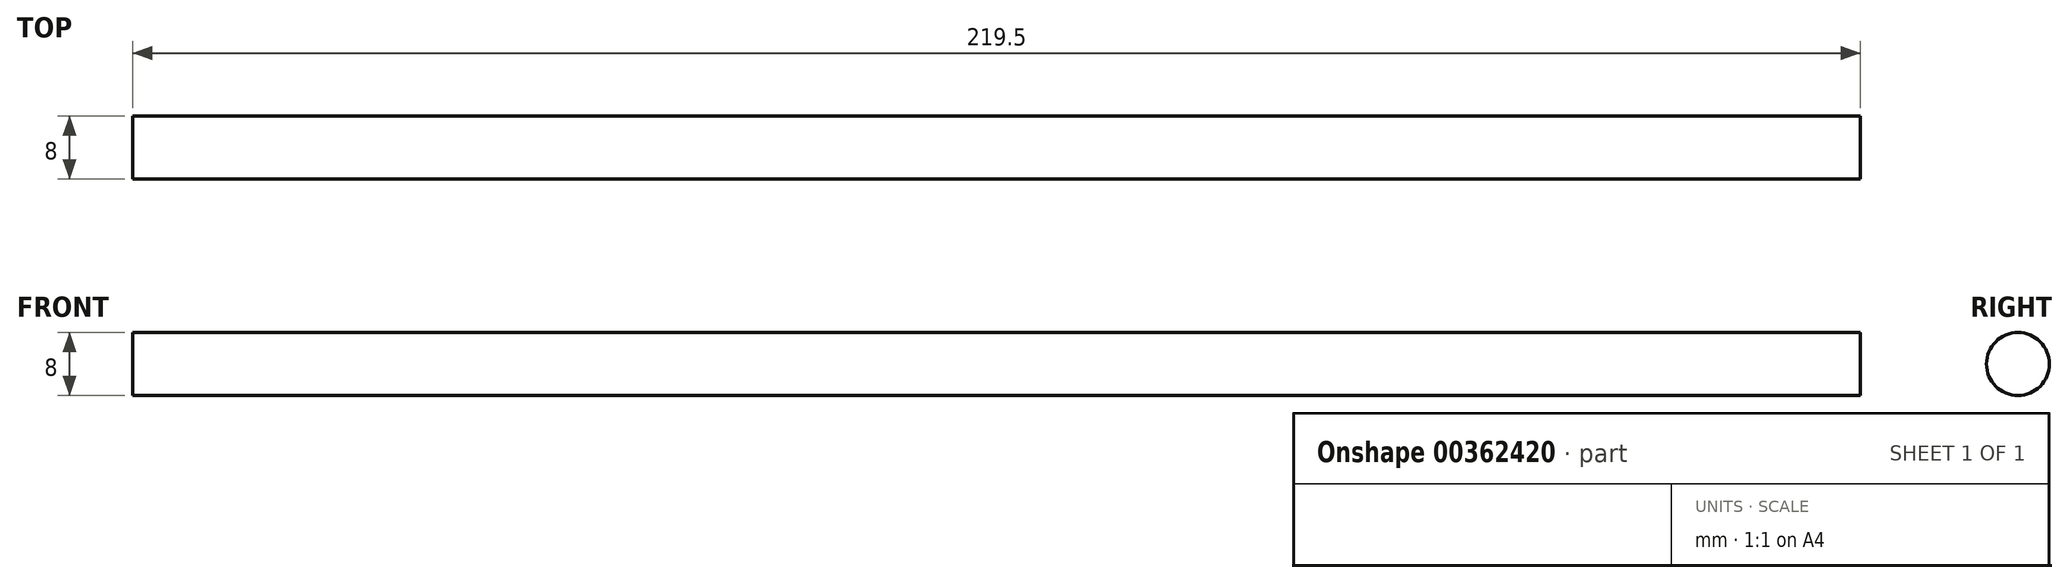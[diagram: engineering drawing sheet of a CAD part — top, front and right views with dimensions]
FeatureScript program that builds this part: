
annotation { "Feature Type Name" : "Feature", "Feature Type Description" : "" }
export const myFeature = defineFeature(function(context is Context, id is Id, definition is map)
    precondition{}
    {
        {
            var Q0;
            Q0=qCreatedBy(makeId("Right.planeOp"),FACE);
            var sketch = newSketch(context, id + "F0", { "sketchPlane" : qUnion([Q0])});
            skCircle(sketch, "E0", {"center": v(0, 0) * mm, "radius": 4 * mm});
            skSolve(sketch);
        }
        {
            var Q0;
            Q0=makeQuery(id+"F0.imprint","IMPRINT",FACE,{"disambiguationData":[TD([[makeQuery(id+"F0.imprint","IMPRINT",EDGE,{"derivedFrom":sQuery(id+"F0.wireOp",EDGE,"E0")}),1.0]])]});
            extrude(context, id + "F1", {"entities" : qUnion([Q0]), "endBound" : BoundingType.SYMMETRIC, "depth" : 219.5 * mm});
        }
    });
